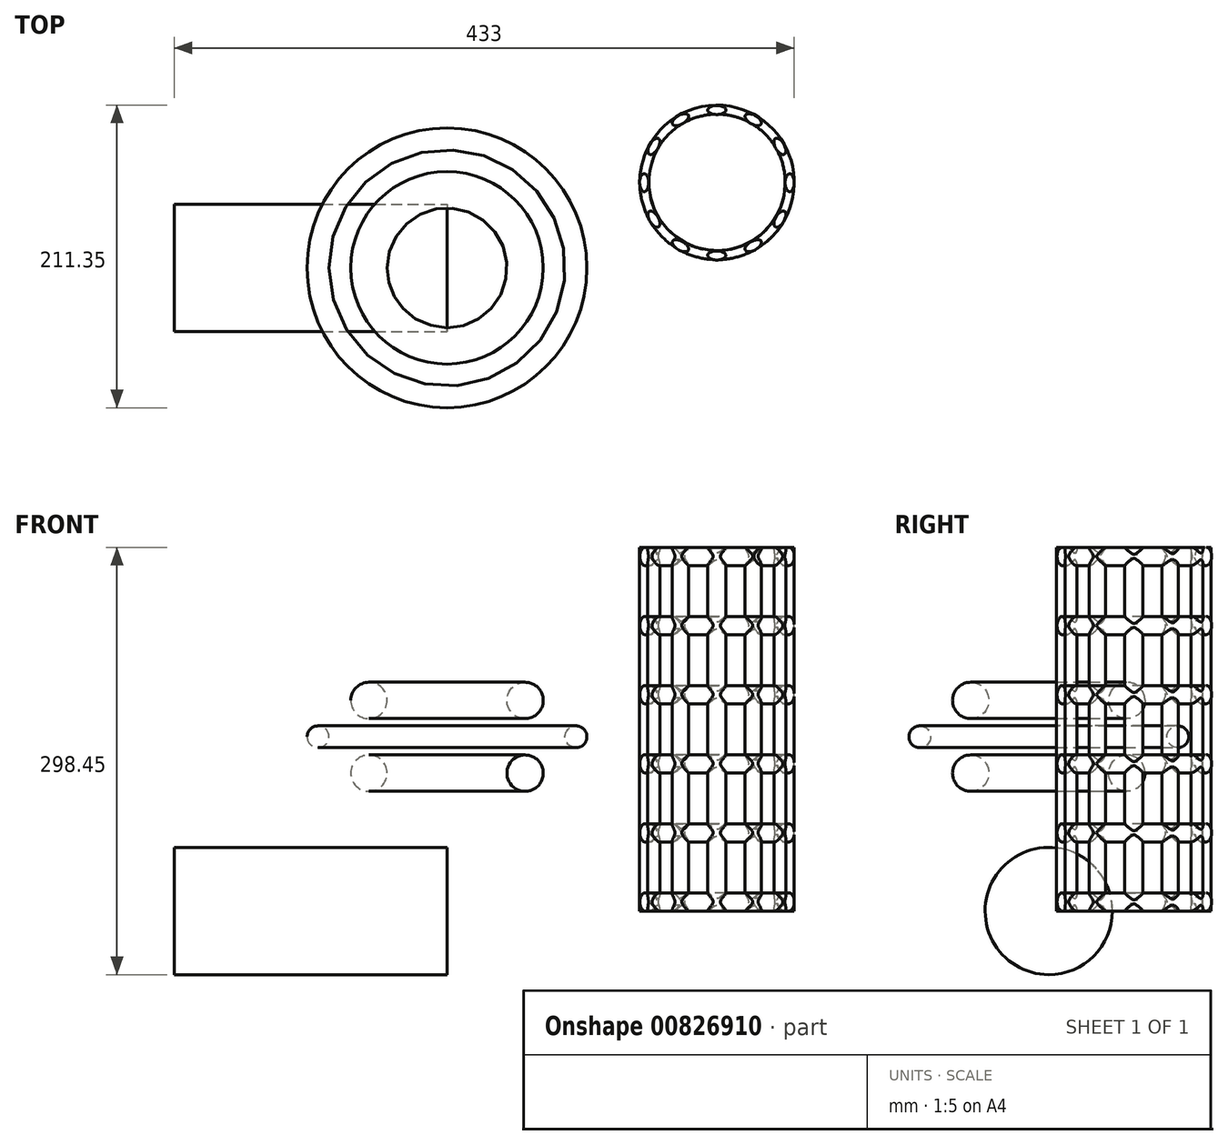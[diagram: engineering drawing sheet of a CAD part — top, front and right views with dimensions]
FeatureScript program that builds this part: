
annotation { "Feature Type Name" : "Feature", "Feature Type Description" : "" }
export const myFeature = defineFeature(function(context is Context, id is Id, definition is map)
    precondition{}
    {
        {
            var Q0;
            Q0=qCreatedBy(makeId("Right.planeOp"),FACE);
            var sketch = newSketch(context, id + "F0", { "sketchPlane" : qUnion([Q0])});
            skCircle(sketch, "E0", {"center": v(0, 0) * mm, "radius": 44.45 * mm});
            skSolve(sketch);
        }
        {
            var Q0;
            Q0=makeQuery(id+"F0.imprint","IMPRINT",FACE,{"disambiguationData":[TD([[makeQuery(id+"F0.imprint","IMPRINT",EDGE,{"derivedFrom":sQuery(id+"F0.wireOp",EDGE,"E0")}),1.0]])]});
            extrude(context, id + "F1", {"entities" : qUnion([Q0]), "oppositeDirection" : true, "depth" : 190.5 * mm, "offsetDistance" : 25.4 * mm});
        }
        {
            var Q0;
            Q0=qCreatedBy(makeId("Right.planeOp"),FACE);
            var sketch = newSketch(context, id + "F2", { "sketchPlane" : qUnion([Q0])});
            skCircle(sketch, "E1", {"center": v(-54.5, 96.27) * mm, "radius": 12.7 * mm});
            skCircle(sketch, "E2", {"center": v(-90.06, 121.67) * mm, "radius": 7.62 * mm});
            skCircle(sketch, "E3", {"center": v(-54.5, 147.07) * mm, "radius": 12.7 * mm});
            skLineSegment(sketch, "E4", {"start": v(0, 15.06) * mm, "end": v(0, 169.71) * mm});
            skSolve(sketch);
        }
        {
            var Q0;
            Q0=makeQuery(id+"F2.imprint","IMPRINT",FACE,{"disambiguationData":[TD([[makeQuery(id+"F2.imprint","IMPRINT",EDGE,{"derivedFrom":sQuery(id+"F2.wireOp",EDGE,"E3")}),1.0]])]});
            var Q1;
            Q1=makeQuery(id+"F2.imprint","IMPRINT",FACE,{"disambiguationData":[TD([[makeQuery(id+"F2.imprint","IMPRINT",EDGE,{"derivedFrom":sQuery(id+"F2.wireOp",EDGE,"E2")}),1.0]])]});
            var Q2;
            Q2=makeQuery(id+"F2.imprint","IMPRINT",FACE,{"disambiguationData":[TD([[makeQuery(id+"F2.imprint","IMPRINT",EDGE,{"derivedFrom":sQuery(id+"F2.wireOp",EDGE,"E1")}),1.0]])]});
            var Q3;
            Q3=sQuery(id+"F2.wireOp",EDGE,"E4");
            revolve(context, id + "F3", {"surfaceOperationType" : NewSurfaceOperationType.NEW, "entities" : qUnion([Q0, Q1, Q2]), "axis" : qUnion([Q3]), "revolveType" : RevolveType.FULL});
        }
        {
            var Q0;
            Q0=qCreatedBy(makeId("Top.planeOp"),FACE);
            var sketch = newSketch(context, id + "F4", { "sketchPlane" : qUnion([Q0])});
            skCircle(sketch, "E5", {"center": v(188.43, 59.46) * mm, "radius": 50.8 * mm});
            skLineSegment(sketch, "E6", {"start": v(188.43, 59.46) * mm, "end": v(188.43, 110.26) * mm});
            skLineSegment(sketch, "E7", {"start": v(188.43, 59.46) * mm, "end": v(188.43, 8.66) * mm});
            skLineSegment(sketch, "E8", {"start": v(188.43, 59.46) * mm, "end": v(239.23, 59.46) * mm});
            skLineSegment(sketch, "E9", {"start": v(188.43, 59.46) * mm, "end": v(137.63, 59.46) * mm});
            skLineSegment(sketch, "E10", {"start": v(188.43, 59.46) * mm, "end": v(133.36, 91.26) * mm});
            skLineSegment(sketch, "E11", {"start": v(188.43, 59.46) * mm, "end": v(156.56, 114.68) * mm});
            skLineSegment(sketch, "E12.MirrorCS", {"start": v(188.77, 60.04) * mm, "end": v(243.7, 28.33) * mm});
            skLineSegment(sketch, "E13.MirrorCS", {"start": v(188.77, 60.04) * mm, "end": v(220.56, 4.96) * mm});
            skLineSegment(sketch, "E14", {"start": v(188.43, 59.46) * mm, "end": v(218.87, 112.18) * mm});
            skLineSegment(sketch, "E15", {"start": v(188.43, 59.46) * mm, "end": v(245.81, 92.6) * mm});
            skLineSegment(sketch, "E16", {"start": v(188.43, 59.46) * mm, "end": v(135.13, 28.69) * mm});
            skLineSegment(sketch, "E17", {"start": v(188.43, 59.46) * mm, "end": v(157.83, 6.46) * mm});
            skEllipse(sketch, "E18", {"center": v(188.38, 110.26) * mm, "majorRadius": 6.35 * mm, "minorRadius": 3.18 * mm, "majorAxis": v(1, 0)});
            skEllipse(sketch, "E19", {"center": v(213.83, 103.46) * mm, "majorRadius": 6.35 * mm, "minorRadius": 3.18 * mm, "majorAxis": v(0.87, -0.5)});
            skEllipse(sketch, "E20", {"center": v(232.43, 84.86) * mm, "majorRadius": 6.35 * mm, "minorRadius": 3.18 * mm, "majorAxis": v(0.5, -0.87)});
            skEllipse(sketch, "E21", {"center": v(239.23, 59.46) * mm, "majorRadius": 6.35 * mm, "minorRadius": 3.18 * mm, "majorAxis": v(0, -1)});
            skEllipse(sketch, "E22.MirrorC", {"center": v(137.63, 59.46) * mm, "majorRadius": 6.35 * mm, "minorRadius": 3.18 * mm, "majorAxis": v(0, -1)});
            skEllipse(sketch, "E23.MirrorC", {"center": v(144.44, 84.86) * mm, "majorRadius": 6.35 * mm, "minorRadius": 3.18 * mm, "majorAxis": v(-0.5, -0.87)});
            skEllipse(sketch, "E24.MirrorC", {"center": v(163.03, 103.46) * mm, "majorRadius": 6.35 * mm, "minorRadius": 3.18 * mm, "majorAxis": v(-0.87, -0.5)});
            skEllipse(sketch, "E25.MirrorC", {"center": v(188.38, 8.66) * mm, "majorRadius": 6.35 * mm, "minorRadius": 3.18 * mm, "majorAxis": v(1, 0)});
            skEllipse(sketch, "E26.MirrorC", {"center": v(213.83, 15.47) * mm, "majorRadius": 6.35 * mm, "minorRadius": 3.18 * mm, "majorAxis": v(0.87, 0.5)});
            skEllipse(sketch, "E27.MirrorC", {"center": v(232.43, 34.06) * mm, "majorRadius": 6.35 * mm, "minorRadius": 3.18 * mm, "majorAxis": v(0.5, 0.87)});
            skEllipse(sketch, "E28.MirrorC", {"center": v(163.03, 15.47) * mm, "majorRadius": 6.35 * mm, "minorRadius": 3.18 * mm, "majorAxis": v(-0.87, 0.5)});
            skEllipse(sketch, "E29.MirrorC", {"center": v(144.44, 34.06) * mm, "majorRadius": 6.35 * mm, "minorRadius": 3.18 * mm, "majorAxis": v(-0.5, 0.87)});
            skSolve(sketch);
        }
        {
            var Q0;
            {var subQ0=sQuery(id+"F4.wireOp",EDGE,"E28.MirrorC");var subQ1=sQuery(id+"F4.wireOp",EDGE,"E5");var subQ2=makeQuery(id+"F4.imprint","INTERSECT",VERTEX,{"disambiguationData":[OD(0.0)],"derivedFrom":[subQ1,subQ0]});Q0=makeQuery(id+"F4.imprint","IMPRINT",FACE,{"disambiguationData":[TD([[makeQuery(id+"F4.imprint","IMPRINT",EDGE,{"disambiguationData":[TD([[subQ2,-1.0]])],"derivedFrom":subQ1}),-1.0]])]});}
            var Q1;
            {var subQ0=sQuery(id+"F4.wireOp",EDGE,"E28.MirrorC");var subQ1=sQuery(id+"F4.wireOp",EDGE,"E5");var subQ2=makeQuery(id+"F4.imprint","INTERSECT",VERTEX,{"disambiguationData":[OD(1.0)],"derivedFrom":[subQ1,subQ0]});Q1=makeQuery(id+"F4.imprint","IMPRINT",FACE,{"disambiguationData":[TD([[makeQuery(id+"F4.imprint","IMPRINT",EDGE,{"disambiguationData":[TD([[subQ2,1.0]])],"derivedFrom":subQ1}),-1.0]])]});}
            var Q2;
            {var subQ0=sQuery(id+"F4.wireOp",EDGE,"E28.MirrorC");var subQ1=sQuery(id+"F4.wireOp",EDGE,"E5");var subQ2=makeQuery(id+"F4.imprint","INTERSECT",VERTEX,{"disambiguationData":[OD(1.0)],"derivedFrom":[subQ1,subQ0]});Q2=makeQuery(id+"F4.imprint","IMPRINT",FACE,{"disambiguationData":[TD([[makeQuery(id+"F4.imprint","IMPRINT",EDGE,{"disambiguationData":[TD([[subQ2,1.0]])],"derivedFrom":subQ1}),1.0]])]});}
            var Q3;
            {var subQ0=sQuery(id+"F4.wireOp",EDGE,"E28.MirrorC");var subQ1=sQuery(id+"F4.wireOp",EDGE,"E5");var subQ2=makeQuery(id+"F4.imprint","INTERSECT",VERTEX,{"disambiguationData":[OD(0.0)],"derivedFrom":[subQ1,subQ0]});Q3=makeQuery(id+"F4.imprint","IMPRINT",FACE,{"disambiguationData":[TD([[makeQuery(id+"F4.imprint","IMPRINT",EDGE,{"disambiguationData":[TD([[subQ2,-1.0]])],"derivedFrom":subQ1}),1.0]])]});}
            var Q4;
            {var subQ0=sQuery(id+"F4.wireOp",EDGE,"E5");var subQ1=makeQuery(id+"F4.imprint","INTERSECT",VERTEX,{"derivedFrom":[subQ0,sQuery(id+"F4.wireOp",EDGE,"E7")]});Q4=makeQuery(id+"F4.imprint","IMPRINT",FACE,{"disambiguationData":[TD([[makeQuery(id+"F4.imprint","IMPRINT",EDGE,{"disambiguationData":[TD([[subQ1,1.0]])],"derivedFrom":subQ0}),-1.0]])]});}
            var Q5;
            {var subQ0=sQuery(id+"F4.wireOp",EDGE,"E7");var subQ1=sQuery(id+"F4.wireOp",EDGE,"E5");var subQ2=makeQuery(id+"F4.imprint","INTERSECT",VERTEX,{"derivedFrom":[subQ1,subQ0]});Q5=makeQuery(id+"F4.imprint","IMPRINT",FACE,{"disambiguationData":[TD([[makeQuery(id+"F4.imprint","IMPRINT",EDGE,{"disambiguationData":[TD([[subQ2,-1.0]])],"derivedFrom":subQ1}),1.0]])]});}
            var Q6;
            {var subQ0=sQuery(id+"F4.wireOp",EDGE,"E7");var subQ1=sQuery(id+"F4.wireOp",EDGE,"E5");var subQ2=makeQuery(id+"F4.imprint","INTERSECT",VERTEX,{"derivedFrom":[subQ1,subQ0]});Q6=makeQuery(id+"F4.imprint","IMPRINT",FACE,{"disambiguationData":[TD([[makeQuery(id+"F4.imprint","IMPRINT",EDGE,{"disambiguationData":[TD([[subQ2,1.0]])],"derivedFrom":subQ1}),1.0]])]});}
            var Q7;
            {var subQ0=sQuery(id+"F4.wireOp",EDGE,"E26.MirrorC");var subQ1=sQuery(id+"F4.wireOp",EDGE,"E5");var subQ2=makeQuery(id+"F4.imprint","INTERSECT",VERTEX,{"disambiguationData":[OD(0.0)],"derivedFrom":[subQ1,subQ0]});Q7=makeQuery(id+"F4.imprint","IMPRINT",FACE,{"disambiguationData":[TD([[makeQuery(id+"F4.imprint","IMPRINT",EDGE,{"disambiguationData":[TD([[subQ2,-1.0]])],"derivedFrom":subQ1}),-1.0]])]});}
            var Q8;
            {var subQ0=sQuery(id+"F4.wireOp",EDGE,"E26.MirrorC");var subQ1=sQuery(id+"F4.wireOp",EDGE,"E5");var subQ2=makeQuery(id+"F4.imprint","INTERSECT",VERTEX,{"disambiguationData":[OD(1.0)],"derivedFrom":[subQ1,subQ0]});Q8=makeQuery(id+"F4.imprint","IMPRINT",FACE,{"disambiguationData":[TD([[makeQuery(id+"F4.imprint","IMPRINT",EDGE,{"disambiguationData":[TD([[subQ2,1.0]])],"derivedFrom":subQ1}),-1.0]])]});}
            var Q9;
            {var subQ0=sQuery(id+"F4.wireOp",EDGE,"E26.MirrorC");var subQ1=sQuery(id+"F4.wireOp",EDGE,"E5");var subQ2=makeQuery(id+"F4.imprint","INTERSECT",VERTEX,{"disambiguationData":[OD(1.0)],"derivedFrom":[subQ1,subQ0]});Q9=makeQuery(id+"F4.imprint","IMPRINT",FACE,{"disambiguationData":[TD([[makeQuery(id+"F4.imprint","IMPRINT",EDGE,{"disambiguationData":[TD([[subQ2,1.0]])],"derivedFrom":subQ1}),1.0]])]});}
            var Q10;
            {var subQ0=sQuery(id+"F4.wireOp",EDGE,"E26.MirrorC");var subQ1=sQuery(id+"F4.wireOp",EDGE,"E5");var subQ2=makeQuery(id+"F4.imprint","INTERSECT",VERTEX,{"disambiguationData":[OD(0.0)],"derivedFrom":[subQ1,subQ0]});Q10=makeQuery(id+"F4.imprint","IMPRINT",FACE,{"disambiguationData":[TD([[makeQuery(id+"F4.imprint","IMPRINT",EDGE,{"disambiguationData":[TD([[subQ2,-1.0]])],"derivedFrom":subQ1}),1.0]])]});}
            var Q11;
            {var subQ0=sQuery(id+"F4.wireOp",EDGE,"E27.MirrorC");var subQ1=sQuery(id+"F4.wireOp",EDGE,"E5");var subQ2=makeQuery(id+"F4.imprint","INTERSECT",VERTEX,{"disambiguationData":[OD(0.0)],"derivedFrom":[subQ1,subQ0]});Q11=makeQuery(id+"F4.imprint","IMPRINT",FACE,{"disambiguationData":[TD([[makeQuery(id+"F4.imprint","IMPRINT",EDGE,{"disambiguationData":[TD([[subQ2,-1.0]])],"derivedFrom":subQ1}),-1.0]])]});}
            var Q12;
            {var subQ0=sQuery(id+"F4.wireOp",EDGE,"E27.MirrorC");var subQ1=sQuery(id+"F4.wireOp",EDGE,"E5");var subQ2=makeQuery(id+"F4.imprint","INTERSECT",VERTEX,{"disambiguationData":[OD(0.0)],"derivedFrom":[subQ1,subQ0]});Q12=makeQuery(id+"F4.imprint","IMPRINT",FACE,{"disambiguationData":[TD([[makeQuery(id+"F4.imprint","IMPRINT",EDGE,{"disambiguationData":[TD([[subQ2,-1.0]])],"derivedFrom":subQ1}),1.0]])]});}
            var Q13;
            {var subQ0=sQuery(id+"F4.wireOp",EDGE,"E27.MirrorC");var subQ1=sQuery(id+"F4.wireOp",EDGE,"E5");var subQ2=makeQuery(id+"F4.imprint","INTERSECT",VERTEX,{"disambiguationData":[OD(1.0)],"derivedFrom":[subQ1,subQ0]});Q13=makeQuery(id+"F4.imprint","IMPRINT",FACE,{"disambiguationData":[TD([[makeQuery(id+"F4.imprint","IMPRINT",EDGE,{"disambiguationData":[TD([[subQ2,1.0]])],"derivedFrom":subQ1}),1.0]])]});}
            var Q14;
            {var subQ0=sQuery(id+"F4.wireOp",EDGE,"E27.MirrorC");var subQ1=sQuery(id+"F4.wireOp",EDGE,"E5");var subQ2=makeQuery(id+"F4.imprint","INTERSECT",VERTEX,{"disambiguationData":[OD(1.0)],"derivedFrom":[subQ1,subQ0]});Q14=makeQuery(id+"F4.imprint","IMPRINT",FACE,{"disambiguationData":[TD([[makeQuery(id+"F4.imprint","IMPRINT",EDGE,{"disambiguationData":[TD([[subQ2,1.0]])],"derivedFrom":subQ1}),-1.0]])]});}
            var Q15;
            {var subQ0=sQuery(id+"F4.wireOp",EDGE,"E8");var subQ1=sQuery(id+"F4.wireOp",EDGE,"E5");var subQ2=makeQuery(id+"F4.imprint","INTERSECT",VERTEX,{"derivedFrom":[subQ1,subQ0]});Q15=makeQuery(id+"F4.imprint","IMPRINT",FACE,{"disambiguationData":[TD([[makeQuery(id+"F4.imprint","IMPRINT",EDGE,{"disambiguationData":[TD([[subQ2,1.0]])],"derivedFrom":subQ1}),1.0]])]});}
            var Q16;
            {var subQ0=sQuery(id+"F4.wireOp",EDGE,"E5");var subQ1=makeQuery(id+"F4.imprint","INTERSECT",VERTEX,{"derivedFrom":[subQ0,sQuery(id+"F4.wireOp",EDGE,"E8")]});Q16=makeQuery(id+"F4.imprint","IMPRINT",FACE,{"disambiguationData":[TD([[makeQuery(id+"F4.imprint","IMPRINT",EDGE,{"disambiguationData":[TD([[subQ1,-1.0]])],"derivedFrom":subQ0}),-1.0]])]});}
            var Q17;
            {var subQ0=sQuery(id+"F4.wireOp",EDGE,"E8");var subQ1=sQuery(id+"F4.wireOp",EDGE,"E5");var subQ2=makeQuery(id+"F4.imprint","INTERSECT",VERTEX,{"derivedFrom":[subQ1,subQ0]});Q17=makeQuery(id+"F4.imprint","IMPRINT",FACE,{"disambiguationData":[TD([[makeQuery(id+"F4.imprint","IMPRINT",EDGE,{"disambiguationData":[TD([[subQ2,-1.0]])],"derivedFrom":subQ1}),1.0]])]});}
            var Q18;
            {var subQ0=sQuery(id+"F4.wireOp",EDGE,"E20");var subQ1=sQuery(id+"F4.wireOp",EDGE,"E5");var subQ2=makeQuery(id+"F4.imprint","INTERSECT",VERTEX,{"disambiguationData":[OD(1.0)],"derivedFrom":[subQ1,subQ0]});Q18=makeQuery(id+"F4.imprint","IMPRINT",FACE,{"disambiguationData":[TD([[makeQuery(id+"F4.imprint","IMPRINT",EDGE,{"disambiguationData":[TD([[subQ2,1.0]])],"derivedFrom":subQ1}),-1.0]])]});}
            var Q19;
            {var subQ0=sQuery(id+"F4.wireOp",EDGE,"E20");var subQ1=sQuery(id+"F4.wireOp",EDGE,"E5");var subQ2=makeQuery(id+"F4.imprint","INTERSECT",VERTEX,{"disambiguationData":[OD(1.0)],"derivedFrom":[subQ1,subQ0]});Q19=makeQuery(id+"F4.imprint","IMPRINT",FACE,{"disambiguationData":[TD([[makeQuery(id+"F4.imprint","IMPRINT",EDGE,{"disambiguationData":[TD([[subQ2,1.0]])],"derivedFrom":subQ1}),1.0]])]});}
            var Q20;
            {var subQ0=sQuery(id+"F4.wireOp",EDGE,"E20");var subQ1=sQuery(id+"F4.wireOp",EDGE,"E5");var subQ2=makeQuery(id+"F4.imprint","INTERSECT",VERTEX,{"disambiguationData":[OD(0.0)],"derivedFrom":[subQ1,subQ0]});Q20=makeQuery(id+"F4.imprint","IMPRINT",FACE,{"disambiguationData":[TD([[makeQuery(id+"F4.imprint","IMPRINT",EDGE,{"disambiguationData":[TD([[subQ2,-1.0]])],"derivedFrom":subQ1}),-1.0]])]});}
            var Q21;
            {var subQ0=sQuery(id+"F4.wireOp",EDGE,"E20");var subQ1=sQuery(id+"F4.wireOp",EDGE,"E5");var subQ2=makeQuery(id+"F4.imprint","INTERSECT",VERTEX,{"disambiguationData":[OD(0.0)],"derivedFrom":[subQ1,subQ0]});Q21=makeQuery(id+"F4.imprint","IMPRINT",FACE,{"disambiguationData":[TD([[makeQuery(id+"F4.imprint","IMPRINT",EDGE,{"disambiguationData":[TD([[subQ2,-1.0]])],"derivedFrom":subQ1}),1.0]])]});}
            var Q22;
            {var subQ0=sQuery(id+"F4.wireOp",EDGE,"E19");var subQ1=sQuery(id+"F4.wireOp",EDGE,"E5");var subQ2=makeQuery(id+"F4.imprint","INTERSECT",VERTEX,{"disambiguationData":[OD(0.0)],"derivedFrom":[subQ1,subQ0]});Q22=makeQuery(id+"F4.imprint","IMPRINT",FACE,{"disambiguationData":[TD([[makeQuery(id+"F4.imprint","IMPRINT",EDGE,{"disambiguationData":[TD([[subQ2,-1.0]])],"derivedFrom":subQ1}),-1.0]])]});}
            var Q23;
            {var subQ0=sQuery(id+"F4.wireOp",EDGE,"E19");var subQ1=sQuery(id+"F4.wireOp",EDGE,"E5");var subQ2=makeQuery(id+"F4.imprint","INTERSECT",VERTEX,{"disambiguationData":[OD(1.0)],"derivedFrom":[subQ1,subQ0]});Q23=makeQuery(id+"F4.imprint","IMPRINT",FACE,{"disambiguationData":[TD([[makeQuery(id+"F4.imprint","IMPRINT",EDGE,{"disambiguationData":[TD([[subQ2,1.0]])],"derivedFrom":subQ1}),-1.0]])]});}
            var Q24;
            {var subQ0=sQuery(id+"F4.wireOp",EDGE,"E19");var subQ1=sQuery(id+"F4.wireOp",EDGE,"E5");var subQ2=makeQuery(id+"F4.imprint","INTERSECT",VERTEX,{"disambiguationData":[OD(1.0)],"derivedFrom":[subQ1,subQ0]});Q24=makeQuery(id+"F4.imprint","IMPRINT",FACE,{"disambiguationData":[TD([[makeQuery(id+"F4.imprint","IMPRINT",EDGE,{"disambiguationData":[TD([[subQ2,1.0]])],"derivedFrom":subQ1}),1.0]])]});}
            var Q25;
            {var subQ0=sQuery(id+"F4.wireOp",EDGE,"E19");var subQ1=sQuery(id+"F4.wireOp",EDGE,"E5");var subQ2=makeQuery(id+"F4.imprint","INTERSECT",VERTEX,{"disambiguationData":[OD(0.0)],"derivedFrom":[subQ1,subQ0]});Q25=makeQuery(id+"F4.imprint","IMPRINT",FACE,{"disambiguationData":[TD([[makeQuery(id+"F4.imprint","IMPRINT",EDGE,{"disambiguationData":[TD([[subQ2,-1.0]])],"derivedFrom":subQ1}),1.0]])]});}
            var Q26;
            {var subQ0=sQuery(id+"F4.wireOp",EDGE,"E6");var subQ1=sQuery(id+"F4.wireOp",EDGE,"E5");var subQ2=makeQuery(id+"F4.imprint","INTERSECT",VERTEX,{"derivedFrom":[subQ1,subQ0]});Q26=makeQuery(id+"F4.imprint","IMPRINT",FACE,{"disambiguationData":[TD([[makeQuery(id+"F4.imprint","IMPRINT",EDGE,{"disambiguationData":[TD([[subQ2,1.0]])],"derivedFrom":subQ1}),1.0]])]});}
            var Q27;
            {var subQ0=sQuery(id+"F4.wireOp",EDGE,"E6");var subQ1=sQuery(id+"F4.wireOp",EDGE,"E5");var subQ2=makeQuery(id+"F4.imprint","INTERSECT",VERTEX,{"derivedFrom":[subQ1,subQ0]});Q27=makeQuery(id+"F4.imprint","IMPRINT",FACE,{"disambiguationData":[TD([[makeQuery(id+"F4.imprint","IMPRINT",EDGE,{"disambiguationData":[TD([[subQ2,-1.0]])],"derivedFrom":subQ1}),1.0]])]});}
            var Q28;
            {var subQ0=sQuery(id+"F4.wireOp",EDGE,"E5");var subQ1=makeQuery(id+"F4.imprint","INTERSECT",VERTEX,{"derivedFrom":[subQ0,sQuery(id+"F4.wireOp",EDGE,"E6")]});Q28=makeQuery(id+"F4.imprint","IMPRINT",FACE,{"disambiguationData":[TD([[makeQuery(id+"F4.imprint","IMPRINT",EDGE,{"disambiguationData":[TD([[subQ1,1.0]])],"derivedFrom":subQ0}),-1.0]])]});}
            var Q29;
            {var subQ0=sQuery(id+"F4.wireOp",EDGE,"E24.MirrorC");var subQ1=sQuery(id+"F4.wireOp",EDGE,"E5");var subQ2=makeQuery(id+"F4.imprint","INTERSECT",VERTEX,{"disambiguationData":[OD(1.0)],"derivedFrom":[subQ1,subQ0]});Q29=makeQuery(id+"F4.imprint","IMPRINT",FACE,{"disambiguationData":[TD([[makeQuery(id+"F4.imprint","IMPRINT",EDGE,{"disambiguationData":[TD([[subQ2,1.0]])],"derivedFrom":subQ1}),-1.0]])]});}
            var Q30;
            {var subQ0=sQuery(id+"F4.wireOp",EDGE,"E24.MirrorC");var subQ1=sQuery(id+"F4.wireOp",EDGE,"E5");var subQ2=makeQuery(id+"F4.imprint","INTERSECT",VERTEX,{"disambiguationData":[OD(0.0)],"derivedFrom":[subQ1,subQ0]});Q30=makeQuery(id+"F4.imprint","IMPRINT",FACE,{"disambiguationData":[TD([[makeQuery(id+"F4.imprint","IMPRINT",EDGE,{"disambiguationData":[TD([[subQ2,-1.0]])],"derivedFrom":subQ1}),-1.0]])]});}
            var Q31;
            {var subQ0=sQuery(id+"F4.wireOp",EDGE,"E24.MirrorC");var subQ1=sQuery(id+"F4.wireOp",EDGE,"E5");var subQ2=makeQuery(id+"F4.imprint","INTERSECT",VERTEX,{"disambiguationData":[OD(0.0)],"derivedFrom":[subQ1,subQ0]});Q31=makeQuery(id+"F4.imprint","IMPRINT",FACE,{"disambiguationData":[TD([[makeQuery(id+"F4.imprint","IMPRINT",EDGE,{"disambiguationData":[TD([[subQ2,-1.0]])],"derivedFrom":subQ1}),1.0]])]});}
            var Q32;
            {var subQ0=sQuery(id+"F4.wireOp",EDGE,"E24.MirrorC");var subQ1=sQuery(id+"F4.wireOp",EDGE,"E5");var subQ2=makeQuery(id+"F4.imprint","INTERSECT",VERTEX,{"disambiguationData":[OD(1.0)],"derivedFrom":[subQ1,subQ0]});Q32=makeQuery(id+"F4.imprint","IMPRINT",FACE,{"disambiguationData":[TD([[makeQuery(id+"F4.imprint","IMPRINT",EDGE,{"disambiguationData":[TD([[subQ2,1.0]])],"derivedFrom":subQ1}),1.0]])]});}
            var Q33;
            {var subQ0=sQuery(id+"F4.wireOp",EDGE,"E23.MirrorC");var subQ1=sQuery(id+"F4.wireOp",EDGE,"E5");var subQ2=makeQuery(id+"F4.imprint","INTERSECT",VERTEX,{"disambiguationData":[OD(0.0)],"derivedFrom":[subQ1,subQ0]});Q33=makeQuery(id+"F4.imprint","IMPRINT",FACE,{"disambiguationData":[TD([[makeQuery(id+"F4.imprint","IMPRINT",EDGE,{"disambiguationData":[TD([[subQ2,-1.0]])],"derivedFrom":subQ1}),-1.0]])]});}
            var Q34;
            {var subQ0=sQuery(id+"F4.wireOp",EDGE,"E23.MirrorC");var subQ1=sQuery(id+"F4.wireOp",EDGE,"E5");var subQ2=makeQuery(id+"F4.imprint","INTERSECT",VERTEX,{"disambiguationData":[OD(0.0)],"derivedFrom":[subQ1,subQ0]});Q34=makeQuery(id+"F4.imprint","IMPRINT",FACE,{"disambiguationData":[TD([[makeQuery(id+"F4.imprint","IMPRINT",EDGE,{"disambiguationData":[TD([[subQ2,-1.0]])],"derivedFrom":subQ1}),1.0]])]});}
            var Q35;
            {var subQ0=sQuery(id+"F4.wireOp",EDGE,"E23.MirrorC");var subQ1=sQuery(id+"F4.wireOp",EDGE,"E5");var subQ2=makeQuery(id+"F4.imprint","INTERSECT",VERTEX,{"disambiguationData":[OD(1.0)],"derivedFrom":[subQ1,subQ0]});Q35=makeQuery(id+"F4.imprint","IMPRINT",FACE,{"disambiguationData":[TD([[makeQuery(id+"F4.imprint","IMPRINT",EDGE,{"disambiguationData":[TD([[subQ2,1.0]])],"derivedFrom":subQ1}),-1.0]])]});}
            var Q36;
            {var subQ0=sQuery(id+"F4.wireOp",EDGE,"E23.MirrorC");var subQ1=sQuery(id+"F4.wireOp",EDGE,"E5");var subQ2=makeQuery(id+"F4.imprint","INTERSECT",VERTEX,{"disambiguationData":[OD(1.0)],"derivedFrom":[subQ1,subQ0]});Q36=makeQuery(id+"F4.imprint","IMPRINT",FACE,{"disambiguationData":[TD([[makeQuery(id+"F4.imprint","IMPRINT",EDGE,{"disambiguationData":[TD([[subQ2,1.0]])],"derivedFrom":subQ1}),1.0]])]});}
            var Q37;
            {var subQ0=sQuery(id+"F4.wireOp",EDGE,"E5");var subQ1=makeQuery(id+"F4.imprint","INTERSECT",VERTEX,{"derivedFrom":[subQ0,sQuery(id+"F4.wireOp",EDGE,"E9")]});Q37=makeQuery(id+"F4.imprint","IMPRINT",FACE,{"disambiguationData":[TD([[makeQuery(id+"F4.imprint","IMPRINT",EDGE,{"disambiguationData":[TD([[subQ1,1.0]])],"derivedFrom":subQ0}),-1.0]])]});}
            var Q38;
            {var subQ0=sQuery(id+"F4.wireOp",EDGE,"E9");var subQ1=sQuery(id+"F4.wireOp",EDGE,"E5");var subQ2=makeQuery(id+"F4.imprint","INTERSECT",VERTEX,{"derivedFrom":[subQ1,subQ0]});Q38=makeQuery(id+"F4.imprint","IMPRINT",FACE,{"disambiguationData":[TD([[makeQuery(id+"F4.imprint","IMPRINT",EDGE,{"disambiguationData":[TD([[subQ2,1.0]])],"derivedFrom":subQ1}),1.0]])]});}
            var Q39;
            {var subQ0=sQuery(id+"F4.wireOp",EDGE,"E9");var subQ1=sQuery(id+"F4.wireOp",EDGE,"E5");var subQ2=makeQuery(id+"F4.imprint","INTERSECT",VERTEX,{"derivedFrom":[subQ1,subQ0]});Q39=makeQuery(id+"F4.imprint","IMPRINT",FACE,{"disambiguationData":[TD([[makeQuery(id+"F4.imprint","IMPRINT",EDGE,{"disambiguationData":[TD([[subQ2,-1.0]])],"derivedFrom":subQ1}),1.0]])]});}
            var Q40;
            {var subQ0=sQuery(id+"F4.wireOp",EDGE,"E29.MirrorC");var subQ1=sQuery(id+"F4.wireOp",EDGE,"E5");var subQ2=makeQuery(id+"F4.imprint","INTERSECT",VERTEX,{"disambiguationData":[OD(0.0)],"derivedFrom":[subQ1,subQ0]});Q40=makeQuery(id+"F4.imprint","IMPRINT",FACE,{"disambiguationData":[TD([[makeQuery(id+"F4.imprint","IMPRINT",EDGE,{"disambiguationData":[TD([[subQ2,-1.0]])],"derivedFrom":subQ1}),-1.0]])]});}
            var Q41;
            {var subQ0=sQuery(id+"F4.wireOp",EDGE,"E29.MirrorC");var subQ1=sQuery(id+"F4.wireOp",EDGE,"E5");var subQ2=makeQuery(id+"F4.imprint","INTERSECT",VERTEX,{"disambiguationData":[OD(1.0)],"derivedFrom":[subQ1,subQ0]});Q41=makeQuery(id+"F4.imprint","IMPRINT",FACE,{"disambiguationData":[TD([[makeQuery(id+"F4.imprint","IMPRINT",EDGE,{"disambiguationData":[TD([[subQ2,1.0]])],"derivedFrom":subQ1}),-1.0]])]});}
            var Q42;
            {var subQ0=sQuery(id+"F4.wireOp",EDGE,"E29.MirrorC");var subQ1=sQuery(id+"F4.wireOp",EDGE,"E5");var subQ2=makeQuery(id+"F4.imprint","INTERSECT",VERTEX,{"disambiguationData":[OD(1.0)],"derivedFrom":[subQ1,subQ0]});Q42=makeQuery(id+"F4.imprint","IMPRINT",FACE,{"disambiguationData":[TD([[makeQuery(id+"F4.imprint","IMPRINT",EDGE,{"disambiguationData":[TD([[subQ2,1.0]])],"derivedFrom":subQ1}),1.0]])]});}
            var Q43;
            {var subQ0=sQuery(id+"F4.wireOp",EDGE,"E29.MirrorC");var subQ1=sQuery(id+"F4.wireOp",EDGE,"E5");var subQ2=makeQuery(id+"F4.imprint","INTERSECT",VERTEX,{"disambiguationData":[OD(0.0)],"derivedFrom":[subQ1,subQ0]});Q43=makeQuery(id+"F4.imprint","IMPRINT",FACE,{"disambiguationData":[TD([[makeQuery(id+"F4.imprint","IMPRINT",EDGE,{"disambiguationData":[TD([[subQ2,-1.0]])],"derivedFrom":subQ1}),1.0]])]});}
            extrude(context, id + "F5", {"entities" : qUnion([Q0, Q1, Q2, Q3, Q4, Q5, Q6, Q7, Q8, Q9, Q10, Q11, Q12, Q13, Q14, Q15, Q16, Q17, Q18, Q19, Q20, Q21, Q22, Q23, Q24, Q25, Q26, Q27, Q28, Q29, Q30, Q31, Q32, Q33, Q34, Q35, Q36, Q37, Q38, Q39, Q40, Q41, Q42, Q43]), "depth" : 254 * mm, "offsetDistance" : 25.4 * mm});
        }
        {
            var Q0;
            Q0=qCreatedBy(makeId("Front.planeOp"),FACE);
            cPlane(context, id + "F6", {"entities" : qUnion([Q0]), "cplaneType" : CPlaneType.OFFSET, "offset" : 59.69 * mm, "oppositeDirection" : true, "width" : 152.4 * mm, "height" : 152.4 * mm});
        }
        {
            var Q0;
            Q0=qCreatedBy(id+"F6.planeOp",FACE);
            var sketch = newSketch(context, id + "F7", { "sketchPlane" : qUnion([Q0])});
            skEllipse(sketch, "E30", {"center": v(137.72, 247.65) * mm, "majorRadius": 6.35 * mm, "minorRadius": 3.18 * mm, "majorAxis": v(0, 1)});
            skLineSegment(sketch, "E31", {"start": v(137.72, 247.65) * mm, "end": v(188.52, 247.65) * mm});
            skLineSegment(sketch, "E32", {"start": v(188.52, 247.65) * mm, "end": v(188.52, 101) * mm});
            skLineSegment(sketch, "E33", {"start": v(137.72, 254) * mm, "end": v(137.72, 0) * mm});
            skEllipse(sketch, "E34", {"center": v(137.72, 199.4) * mm, "majorRadius": 6.35 * mm, "minorRadius": 3.18 * mm, "majorAxis": v(0, 1)});
            skEllipse(sketch, "E35", {"center": v(137.72, 151.13) * mm, "majorRadius": 6.35 * mm, "minorRadius": 3.18 * mm, "majorAxis": v(0, 1)});
            skEllipse(sketch, "E36", {"center": v(137.72, 102.87) * mm, "majorRadius": 6.35 * mm, "minorRadius": 3.18 * mm, "majorAxis": v(0, 1)});
            skEllipse(sketch, "E37", {"center": v(137.72, 54.61) * mm, "majorRadius": 6.35 * mm, "minorRadius": 3.18 * mm, "majorAxis": v(0, 1)});
            skEllipse(sketch, "E38", {"center": v(137.72, 6.35) * mm, "majorRadius": 6.35 * mm, "minorRadius": 3.18 * mm, "majorAxis": v(0, 1)});
            skSolve(sketch);
        }
        {
            var Q0;
            Q0 = qSketchRegion(id + "F7", true);
            var Q1;
            Q1=sQuery(id+"F7.wireOp",EDGE,"E32");
            revolve(context, id + "F8", {"operationType" : NewBodyOperationType.ADD, "surfaceOperationType" : NewSurfaceOperationType.NEW, "entities" : qUnion([Q0]), "axis" : qUnion([Q1]), "revolveType" : RevolveType.FULL});
        }
    });
